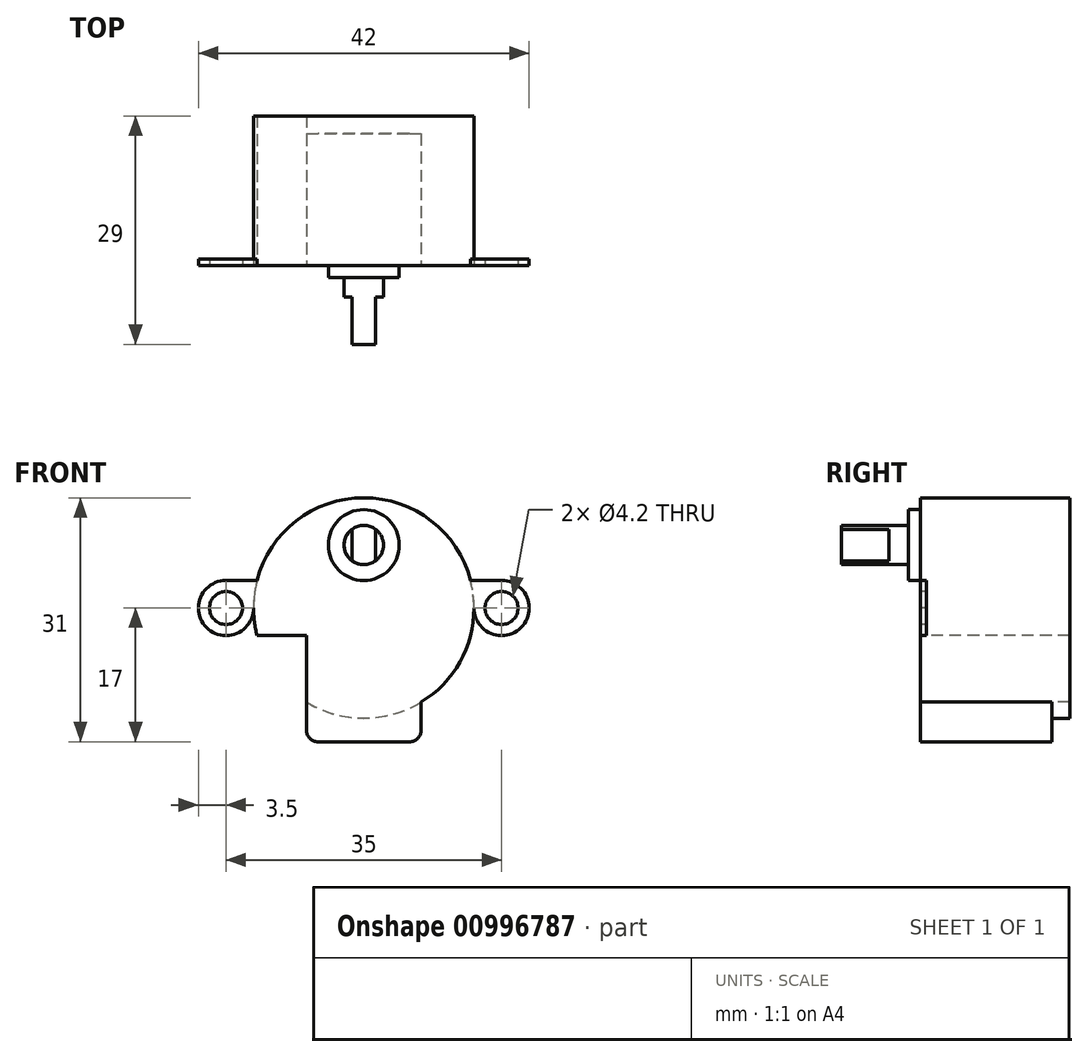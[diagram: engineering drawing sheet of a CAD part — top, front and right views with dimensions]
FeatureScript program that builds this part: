
annotation { "Feature Type Name" : "Feature", "Feature Type Description" : "" }
export const myFeature = defineFeature(function(context is Context, id is Id, definition is map)
    precondition{}
    {
        {
            var Q0;
            Q0=qCreatedBy(makeId("Front.planeOp"),FACE);
            var sketch = newSketch(context, id + "F0", { "sketchPlane" : qUnion([Q0])});
            skCircle(sketch, "E0", {"center": v(0, 0) * mm, "radius": 14 * mm});
            skCircle(sketch, "E1", {"center": v(0, 8) * mm, "radius": 4.5 * mm});
            skCircle(sketch, "E2", {"center": v(-17.5, 0) * mm, "radius": 2.1 * mm});
            skCircle(sketch, "E3", {"center": v(-17.5, 0) * mm, "radius": 3.5 * mm});
            skCircle(sketch, "E4", {"center": v(17.5, 0) * mm, "radius": 2.1 * mm});
            skCircle(sketch, "E5", {"center": v(17.5, 0) * mm, "radius": 3.5 * mm});
            skLineSegment(sketch, "E6", {"start": v(17.5, 3.5) * mm, "end": v(-17.5, 3.5) * mm});
            skLineSegment(sketch, "E7", {"start": v(-17.5, -3.5) * mm, "end": v(17.5, -3.5) * mm});
            skCircle(sketch, "E8", {"center": v(0, 8) * mm, "radius": 2.5 * mm});
            skLineSegment(sketch, "E9", {"start": v(0, 8) * mm, "end": v(1.5, 8) * mm, "construction": true});
            skLineSegment(sketch, "E10", {"start": v(0, 8) * mm, "end": v(-1.5, 8) * mm, "construction": true});
            skLineSegment(sketch, "E11", {"start": v(-1.5, 6) * mm, "end": v(-1.5, 10) * mm});
            skLineSegment(sketch, "E12", {"start": v(1.5, 10) * mm, "end": v(1.5, 6) * mm});
            skLineSegment(sketch, "E13", {"start": v(0, 0) * mm, "end": v(7.3, 0) * mm, "construction": true});
            skLineSegment(sketch, "E14.bottom", {"start": v(7.3, 0) * mm, "end": v(-7.3, 0) * mm, "construction": true});
            skLineSegment(sketch, "E14.top", {"start": v(7.3, -17) * mm, "end": v(-7.3, -17) * mm});
            skLineSegment(sketch, "E14.left", {"start": v(7.3, 0) * mm, "end": v(7.3, -17) * mm});
            skLineSegment(sketch, "E14.right", {"start": v(-7.3, 0) * mm, "end": v(-7.3, -17) * mm});
            skLineSegment(sketch, "E15", {"start": v(0, 0) * mm, "end": v(0, 8) * mm});
            skLineSegment(sketch, "E16", {"start": v(0, 0) * mm, "end": v(17.5, 0) * mm, "construction": true});
            skLineSegment(sketch, "E17", {"start": v(0, 0) * mm, "end": v(-17.5, 0) * mm, "construction": true});
            skSolve(sketch);
        }
        {
            var Q0;
            Q0=makeQuery(id+"F0.imprint","IMPRINT",FACE,{"disambiguationData":[TD([[makeQuery(id+"F0.imprint","IMPRINT",EDGE,{"derivedFrom":sQuery(id+"F0.wireOp",EDGE,"E1")}),1.0]])]});
            extrude(context, id + "F1", {"entities" : qUnion([Q0]), "depth" : 1.5 * mm, "offsetDistance" : 25 * mm});
        }
        {
            var Q0;
            Q0=makeQuery(id+"F0.imprint","IMPRINT",FACE,{"disambiguationData":[TD([[makeQuery(id+"F0.imprint","IMPRINT",EDGE,{"derivedFrom":sQuery(id+"F0.wireOp",EDGE,"E1")}),-1.0]])]});
            var Q1;
            {var subQ1=sQuery(id+"F0.wireOp",EDGE,"E0");var subQ8=sQuery(id+"F0.wireOp",EDGE,"E6");var subQ11=makeQuery(id+"F0.imprint","INTERSECT",VERTEX,{"disambiguationData":[OD(0.0)],"derivedFrom":[subQ1,subQ8]});Q1=makeQuery(id+"F0.imprint","IMPRINT",FACE,{"disambiguationData":[TD([[makeQuery(id+"F0.imprint","IMPRINT",EDGE,{"disambiguationData":[TD([[subQ11,1.0]])],"derivedFrom":subQ1}),1.0]])]});}
            var Q2;
            {var subQ0=sQuery(id+"F0.wireOp",EDGE,"E7");var subQ1=sQuery(id+"F0.wireOp",EDGE,"E0");var subQ2=makeQuery(id+"F0.imprint","INTERSECT",VERTEX,{"disambiguationData":[OD(0.0)],"derivedFrom":[subQ1,subQ0]});Q2=makeQuery(id+"F0.imprint","IMPRINT",FACE,{"disambiguationData":[TD([[makeQuery(id+"F0.imprint","IMPRINT",EDGE,{"disambiguationData":[TD([[subQ2,-1.0]])],"derivedFrom":subQ1}),1.0]])]});}
            var Q3;
            Q3=makeQuery(id+"F0.imprint","IMPRINT",FACE,{"disambiguationData":[TD([[makeQuery(id+"F0.imprint","IMPRINT",EDGE,{"derivedFrom":sQuery(id+"F0.wireOp",EDGE,"E1")}),1.0]])]});
            var Q4;
            {var subQ0=sQuery(id+"F0.wireOp",EDGE,"E11");Q4=makeQuery(id+"F0.imprint","IMPRINT",FACE,{"disambiguationData":[TD([[makeQuery(id+"F0.imprint","IMPRINT",EDGE,{"derivedFrom":subQ0}),1.0]])]});}
            var Q5;
            {var subQ0=sQuery(id+"F0.wireOp",EDGE,"E12");Q5=makeQuery(id+"F0.imprint","IMPRINT",FACE,{"disambiguationData":[TD([[makeQuery(id+"F0.imprint","IMPRINT",EDGE,{"derivedFrom":subQ0}),1.0]])]});}
            var Q6;
            {var subQ0=sQuery(id+"F0.wireOp",EDGE,"E11");Q6=makeQuery(id+"F0.imprint","IMPRINT",FACE,{"disambiguationData":[TD([[makeQuery(id+"F0.imprint","IMPRINT",EDGE,{"derivedFrom":subQ0}),-1.0]])]});}
            var Q7;
            {var subQ0=sQuery(id+"F0.wireOp",EDGE,"E5");var subQ1=sQuery(id+"F0.wireOp",EDGE,"E0");var subQ2=makeQuery(id+"F0.imprint","INTERSECT",VERTEX,{"disambiguationData":[OD(0.0)],"derivedFrom":[subQ1,subQ0]});Q7=makeQuery(id+"F0.imprint","IMPRINT",FACE,{"disambiguationData":[TD([[makeQuery(id+"F0.imprint","IMPRINT",EDGE,{"disambiguationData":[TD([[subQ2,1.0]])],"derivedFrom":subQ1}),1.0]])]});}
            var Q8;
            {var subQ0=sQuery(id+"F0.wireOp",EDGE,"E3");var subQ1=sQuery(id+"F0.wireOp",EDGE,"E0");var subQ2=makeQuery(id+"F0.imprint","INTERSECT",VERTEX,{"disambiguationData":[OD(0.0)],"derivedFrom":[subQ1,subQ0]});Q8=makeQuery(id+"F0.imprint","IMPRINT",FACE,{"disambiguationData":[TD([[makeQuery(id+"F0.imprint","IMPRINT",EDGE,{"disambiguationData":[TD([[subQ2,-1.0]])],"derivedFrom":subQ1}),1.0]])]});}
            var Q9;
            {var subQ0=sQuery(id+"F0.wireOp",EDGE,"E14.right");var subQ1=sQuery(id+"F0.wireOp",EDGE,"E0");var subQ2=makeQuery(id+"F0.imprint","INTERSECT",VERTEX,{"derivedFrom":[subQ1,subQ0]});Q9=makeQuery(id+"F0.imprint","IMPRINT",FACE,{"disambiguationData":[TD([[makeQuery(id+"F0.imprint","IMPRINT",EDGE,{"disambiguationData":[TD([[subQ2,-1.0]])],"derivedFrom":subQ1}),1.0]])]});}
            var Q10;
            {var subQ0=sQuery(id+"F0.wireOp",EDGE,"E14.left");var subQ1=sQuery(id+"F0.wireOp",EDGE,"E0");var subQ2=makeQuery(id+"F0.imprint","INTERSECT",VERTEX,{"derivedFrom":[subQ1,subQ0]});Q10=makeQuery(id+"F0.imprint","IMPRINT",FACE,{"disambiguationData":[TD([[makeQuery(id+"F0.imprint","IMPRINT",EDGE,{"disambiguationData":[TD([[subQ2,-1.0]])],"derivedFrom":subQ1}),1.0]])]});}
            extrude(context, id + "F2", {"entities" : qUnion([Q0, Q1, Q2, Q3, Q4, Q5, Q6, Q7, Q8, Q9, Q10]), "operationType" : NewBodyOperationType.ADD, "oppositeDirection" : true, "depth" : 19 * mm, "offsetDistance" : 25 * mm});
        }
        {
            var Q0;
            Q0=makeQuery(id+"F0.imprint","IMPRINT",FACE,{"disambiguationData":[TD([[makeQuery(id+"F0.imprint","IMPRINT",EDGE,{"derivedFrom":sQuery(id+"F0.wireOp",EDGE,"E2")}),-1.0]])]});
            var Q1;
            {var subQ0=sQuery(id+"F0.wireOp",EDGE,"E6");var subQ1=sQuery(id+"F0.wireOp",EDGE,"E0");var subQ2=makeQuery(id+"F0.imprint","INTERSECT",VERTEX,{"disambiguationData":[OD(1.0)],"derivedFrom":[subQ1,subQ0]});Q1=makeQuery(id+"F0.imprint","IMPRINT",FACE,{"disambiguationData":[TD([[makeQuery(id+"F0.imprint","IMPRINT",EDGE,{"disambiguationData":[TD([[subQ2,-1.0]])],"derivedFrom":subQ1}),-1.0]])]});}
            var Q2;
            {var subQ0=sQuery(id+"F0.wireOp",EDGE,"E7");var subQ1=sQuery(id+"F0.wireOp",EDGE,"E0");var subQ2=makeQuery(id+"F0.imprint","INTERSECT",VERTEX,{"disambiguationData":[OD(0.0)],"derivedFrom":[subQ1,subQ0]});Q2=makeQuery(id+"F0.imprint","IMPRINT",FACE,{"disambiguationData":[TD([[makeQuery(id+"F0.imprint","IMPRINT",EDGE,{"disambiguationData":[TD([[subQ2,1.0]])],"derivedFrom":subQ1}),-1.0]])]});}
            var Q3;
            {var subQ0=sQuery(id+"F0.wireOp",EDGE,"E6");var subQ1=sQuery(id+"F0.wireOp",EDGE,"E0");var subQ2=makeQuery(id+"F0.imprint","INTERSECT",VERTEX,{"disambiguationData":[OD(0.0)],"derivedFrom":[subQ1,subQ0]});Q3=makeQuery(id+"F0.imprint","IMPRINT",FACE,{"disambiguationData":[TD([[makeQuery(id+"F0.imprint","IMPRINT",EDGE,{"disambiguationData":[TD([[subQ2,1.0]])],"derivedFrom":subQ1}),-1.0]])]});}
            var Q4;
            Q4=makeQuery(id+"F0.imprint","IMPRINT",FACE,{"disambiguationData":[TD([[makeQuery(id+"F0.imprint","IMPRINT",EDGE,{"derivedFrom":sQuery(id+"F0.wireOp",EDGE,"E4")}),-1.0]])]});
            var Q5;
            {var subQ0=sQuery(id+"F0.wireOp",EDGE,"E7");var subQ1=sQuery(id+"F0.wireOp",EDGE,"E0");var subQ2=makeQuery(id+"F0.imprint","INTERSECT",VERTEX,{"disambiguationData":[OD(1.0)],"derivedFrom":[subQ1,subQ0]});Q5=makeQuery(id+"F0.imprint","IMPRINT",FACE,{"disambiguationData":[TD([[makeQuery(id+"F0.imprint","IMPRINT",EDGE,{"disambiguationData":[TD([[subQ2,-1.0]])],"derivedFrom":subQ1}),-1.0]])]});}
            extrude(context, id + "F3", {"entities" : qUnion([Q0, Q1, Q2, Q3, Q4, Q5]), "operationType" : NewBodyOperationType.ADD, "oppositeDirection" : true, "depth" : 0.8 * mm, "offsetDistance" : 25 * mm});
        }
        {
            var Q0;
            {var subQ0=sQuery(id+"F0.wireOp",EDGE,"E11");Q0=makeQuery(id+"F0.imprint","IMPRINT",FACE,{"disambiguationData":[TD([[makeQuery(id+"F0.imprint","IMPRINT",EDGE,{"derivedFrom":subQ0}),1.0]])]});}
            var Q1;
            {var subQ0=sQuery(id+"F0.wireOp",EDGE,"E11");Q1=makeQuery(id+"F0.imprint","IMPRINT",FACE,{"disambiguationData":[TD([[makeQuery(id+"F0.imprint","IMPRINT",EDGE,{"derivedFrom":subQ0}),-1.0]])]});}
            var Q2;
            {var subQ0=sQuery(id+"F0.wireOp",EDGE,"E12");Q2=makeQuery(id+"F0.imprint","IMPRINT",FACE,{"disambiguationData":[TD([[makeQuery(id+"F0.imprint","IMPRINT",EDGE,{"derivedFrom":subQ0}),1.0]])]});}
            extrude(context, id + "F4", {"entities" : qUnion([Q0, Q1, Q2]), "depth" : 4 * mm, "offsetDistance" : 25 * mm});
        }
        {
            var Q0;
            {var subQ0=sQuery(id+"F0.wireOp",EDGE,"E11");Q0=makeQuery(id+"F0.imprint","IMPRINT",FACE,{"disambiguationData":[TD([[makeQuery(id+"F0.imprint","IMPRINT",EDGE,{"derivedFrom":subQ0}),-1.0]])]});}
            extrude(context, id + "F5", {"entities" : qUnion([Q0]), "operationType" : NewBodyOperationType.ADD, "depth" : 10 * mm, "offsetDistance" : 25 * mm});
        }
        {
            var Q0;
            {var subQ5=sQuery(id+"F0.wireOp",EDGE,"E14.top");Q0=makeQuery(id+"F0.imprint","IMPRINT",FACE,{"disambiguationData":[TD([[makeQuery(id+"F0.imprint","IMPRINT",EDGE,{"derivedFrom":subQ5}),-1.0]])]});}
            extrude(context, id + "F6", {"entities" : qUnion([Q0]), "operationType" : NewBodyOperationType.ADD, "oppositeDirection" : true, "depth" : 16.75 * mm, "offsetDistance" : 25 * mm});
        }
        {
            var Q0;
            Q0=makeQuery(id+"F6.opExtrude","SWEPT_EDGE",EDGE,{"disambiguationData":[OSD([sQuery(id+"F0.wireOp",EDGE,"E14.top"),sQuery(id+"F0.wireOp",EDGE,"E14.right")])]});
            var Q1;
            Q1=makeQuery(id+"F6.opExtrude","SWEPT_EDGE",EDGE,{"disambiguationData":[OSD([sQuery(id+"F0.wireOp",EDGE,"E14.top"),sQuery(id+"F0.wireOp",EDGE,"E14.left")])]});
            fillet(context, id + "F7", {"entities" : qUnion([Q0, Q1]), "radius" : 1.5 * mm, "tangentPropagation" : true, "allowEdgeOverflow" : false});
        }
    });
